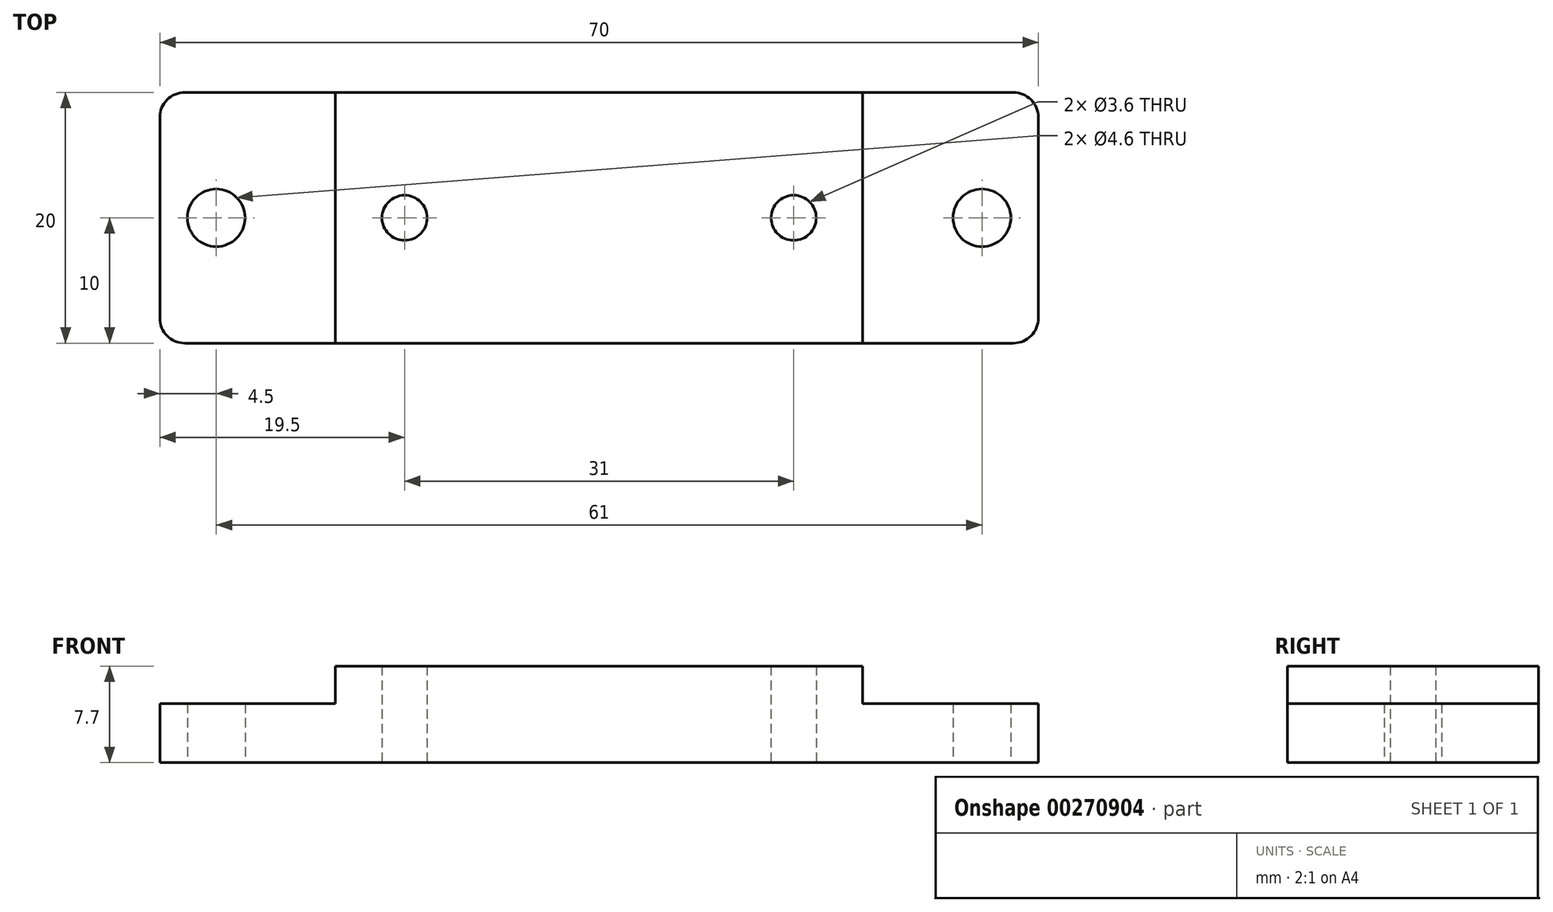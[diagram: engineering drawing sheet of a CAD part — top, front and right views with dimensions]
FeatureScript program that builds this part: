
annotation { "Feature Type Name" : "Feature", "Feature Type Description" : "" }
export const myFeature = defineFeature(function(context is Context, id is Id, definition is map)
    precondition{}
    {
        {
            var Q0;
            Q0=qCreatedBy(makeId("Top.planeOp"),FACE);
            var sketch = newSketch(context, id + "F0", { "sketchPlane" : qUnion([Q0])});
            skLineSegment(sketch, "E0.bottom", {"start": v(-35, 10) * mm, "end": v(35, 10) * mm});
            skLineSegment(sketch, "E0.top", {"start": v(-35, -10) * mm, "end": v(35, -10) * mm});
            skLineSegment(sketch, "E0.left", {"start": v(-35, 10) * mm, "end": v(-35, -10) * mm});
            skLineSegment(sketch, "E0.right", {"start": v(35, 10) * mm, "end": v(35, -10) * mm});
            skPoint(sketch, "E0.middle", {"position": v(0, 0) * mm});
            skPoint(sketch, "E1", {"position": v(-15.5, 0) * mm});
            skPoint(sketch, "E2", {"position": v(15.5, 0) * mm});
            skLineSegment(sketch, "E3", {"start": v(-15.5, 0) * mm, "end": v(15.5, 0) * mm, "construction": true});
            skPoint(sketch, "E4", {"position": v(-30.5, 0) * mm});
            skPoint(sketch, "E5", {"position": v(30.5, 0) * mm});
            skLineSegment(sketch, "E6", {"start": v(-30.5, 0) * mm, "end": v(30.5, 0) * mm});
            skSolve(sketch);
        }
        {
            var Q0;
            Q0 = qSketchRegion(id + "F0", true);
            extrude(context, id + "F1", {"entities" : qUnion([Q0]), "depth" : 4.7 * mm});
        }
        {
            var Q0;
            Q0=makeQuery(id+"F1.opExtrude","CAP_FACE",FACE,{"disambiguationData":[OSD([sQuery(id+"F0.wireOp",EDGE,"E0.bottom"),sQuery(id+"F0.wireOp",EDGE,"E0.top"),sQuery(id+"F0.wireOp",EDGE,"E0.left"),sQuery(id+"F0.wireOp",EDGE,"E0.right")])],"isStart":false});
            var sketch = newSketch(context, id + "F2", { "sketchPlane" : qUnion([Q0])});
            skLineSegment(sketch, "E7.bottom", {"start": v(21, -10) * mm, "end": v(-21, -10) * mm});
            skLineSegment(sketch, "E7.top", {"start": v(21, 10) * mm, "end": v(-21, 10) * mm});
            skLineSegment(sketch, "E7.left", {"start": v(21, -10) * mm, "end": v(21, 10) * mm});
            skLineSegment(sketch, "E7.right", {"start": v(-21, -10) * mm, "end": v(-21, 10) * mm});
            skPoint(sketch, "E7.middle", {"position": v(0, 0) * mm});
            skSolve(sketch);
        }
        {
            var Q0;
            Q0 = qSketchRegion(id + "F2", true);
            extrude(context, id + "F3", {"entities" : qUnion([Q0]), "operationType" : NewBodyOperationType.ADD, "depth" : 3 * mm});
        }
        {
            var Q0;
            Q0=sQuery(id+"F0.wireOp",VERTEX,"E1");
            var Q1;
            Q1=sQuery(id+"F0.wireOp",VERTEX,"E2");
            var Q2;
            Q2=makeQuery(id+"F1.opExtrude","SWEPT_BODY",BODY,{"disambiguationData":[OSD([sQuery(id+"F0.wireOp",EDGE,"E0.bottom"),sQuery(id+"F0.wireOp",EDGE,"E0.top"),sQuery(id+"F0.wireOp",EDGE,"E0.left"),sQuery(id+"F0.wireOp",EDGE,"E0.right")])]});
            hole(context, id + "F4", {"style" : HoleStyle.SIMPLE, "endStyle" : HoleEndStyle.BLIND, "oppositeDirection" : true, "holeDiameter" : 3.6 * mm, "holeDepth" : 12 * mm, "tappedDepth" : 12 * mm, "tapClearance" : 3, "startFromSketch" : true, "locations" : qUnion([Q0, Q1]), "scope" : qUnion([Q2])});
        }
        {
            var Q0;
            Q0=sQuery(id+"F0.wireOp",VERTEX,"E4");
            var Q1;
            Q1=sQuery(id+"F0.wireOp",VERTEX,"E5");
            var Q2;
            Q2=makeQuery(id+"F1.opExtrude","SWEPT_BODY",BODY,{"disambiguationData":[OSD([sQuery(id+"F0.wireOp",EDGE,"E0.bottom"),sQuery(id+"F0.wireOp",EDGE,"E0.top"),sQuery(id+"F0.wireOp",EDGE,"E0.left"),sQuery(id+"F0.wireOp",EDGE,"E0.right")])]});
            hole(context, id + "F5", {"style" : HoleStyle.SIMPLE, "endStyle" : HoleEndStyle.BLIND, "oppositeDirection" : true, "holeDiameter" : 4.6 * mm, "holeDepth" : 12 * mm, "tappedDepth" : 12 * mm, "tapClearance" : 3, "startFromSketch" : true, "locations" : qUnion([Q0, Q1]), "scope" : qUnion([Q2])});
        }
        {
            var Q0;
            Q0=makeQuery(id+"F1.opExtrude","SWEPT_EDGE",EDGE,{"disambiguationData":[OSD([sQuery(id+"F0.wireOp",EDGE,"E0.top"),sQuery(id+"F0.wireOp",EDGE,"E0.right")])]});
            var Q1;
            Q1=makeQuery(id+"F1.opExtrude","SWEPT_EDGE",EDGE,{"disambiguationData":[OSD([sQuery(id+"F0.wireOp",EDGE,"E0.bottom"),sQuery(id+"F0.wireOp",EDGE,"E0.right")])]});
            var Q2;
            Q2=makeQuery(id+"F1.opExtrude","SWEPT_EDGE",EDGE,{"disambiguationData":[OSD([sQuery(id+"F0.wireOp",EDGE,"E0.bottom"),sQuery(id+"F0.wireOp",EDGE,"E0.left")])]});
            var Q3;
            Q3=makeQuery(id+"F1.opExtrude","SWEPT_EDGE",EDGE,{"disambiguationData":[OSD([sQuery(id+"F0.wireOp",EDGE,"E0.top"),sQuery(id+"F0.wireOp",EDGE,"E0.left")])]});
            fillet(context, id + "F6", {"entities" : qUnion([Q0, Q1, Q2, Q3]), "radius" : 2 * mm, "tangentPropagation" : true, "allowEdgeOverflow" : false});
        }
    });
